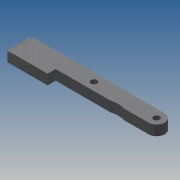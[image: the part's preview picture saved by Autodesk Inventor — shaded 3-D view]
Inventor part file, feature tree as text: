
AUTODESK INVENTOR PART (.ipt)
format: ipt  version: 2015 SP1 (Build 190203100, 203)  size: 134,144 bytes
history: native  units: mm
features: extrude x2, sketch x2, fillet x1, reference x1
ambient origin geometry x8: Origin, YZ Plane, XZ Plane, XY Plane, X Axis, Y Axis, Z Axis, Center Point
bodies: Body1 (feature_tree)
feature tree (6):
  extrude  "Extrusion3"  Depth=15.5mm
  extrude  "Extrusion4"  Depth=2.0mm
  fillet  "Rundung1"  Radius=16.5mm
  sketch  "Skizze1"  dims[d0=3.1mm d1=15.5mm]
  sketch  "Skizze3"  dims[d2=15.5mm d3=22.0mm d4=16.5mm d5=11.0mm d6=8.0mm d7=15.0mm d10=15.0mm d11=40.0mm d17=8.0mm d18=10.0mm d19=8.0mm d20=8.0mm d22=35.0mm d23=15.0mm d24=5.0mm d25=0.0mm d26=5.0mm d27=0.0mm d29=2.0mm]
  reference  "Referenz1"
